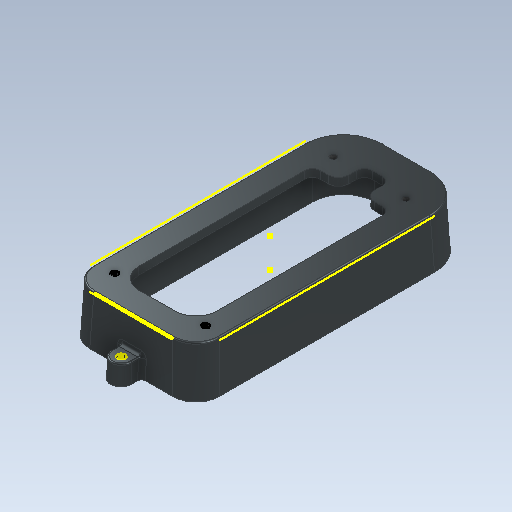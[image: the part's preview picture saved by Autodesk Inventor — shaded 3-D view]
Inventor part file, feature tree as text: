
AUTODESK INVENTOR PART (.ipt)
format: ipt  version: 2020 (Build 240168000, 168)  size: 400,896 bytes
history: native  units: mm
features: fillet x10, sketch x9, move_body x6, extrude x5, direct_edit x5, draft x5, thread x4, hole x2, boolean_combine x2, revolve x2, shell x1
ambient origin geometry x8: Origin, YZ Plane, XZ Plane, XY Plane, X Axis, Y Axis, Z Axis, Center Point
bodies: Solid1 (feature_tree), Solid2 (feature_tree), Solid3 (feature_tree)
feature tree (51):
  extrude  "Extrusion1"  Depth=107.0mm
  extrude  "Extrusion2"  Depth=8.0mm
  direct_edit  "Direct Edit1"
  draft  "FaceDraft1"
  draft  "FaceDraft2"
  direct_edit  "Direct Edit2"
  fillet  "Fillet1"  Radius=8.0mm
  direct_edit  "Direct Edit3"
  extrude  "Extrusion3"  Depth=7.5mm TaperAngle=0.0deg
  fillet  "Fillet2"  [1 undecoded]
  fillet  "Fillet3"  Radius=0.436332mm
  fillet  "Fillet4"  [1 undecoded]
  fillet  "Fillet5"  Radius=4.0mm
  fillet  "Fillet6"  Radius=30.0mm
  fillet  "Fillet7"  Radius=75.0mm
  sketch  "Sketch5"  dims[d10=0.0mm d11=0.0mm d12=5.0mm d13=0.436332mm d14=-0.436332mm]
  shell  "Shell1"  Thickness=10.0mm
  extrude  "Extrusion6"  Depth=10.0mm
  direct_edit  "Direct Edit4"
  draft  "FaceDraft3"
  draft  "FaceDraft4"
  draft  "FaceDraft5"
  direct_edit  "Direct Edit5"
  fillet  "Fillet13"  Radius=10.0mm
  hole  "Hole4"  [1 undecoded]
  sketch  "Sketch11"  dims[d25=10.0mm d26=10.0mm d27=10.0mm]
  extrude  "Extrusion7"  Depth=1.5mm
  fillet  "Fillet14"  Radius=8.0mm
  boolean_combine  "Combine4"
  boolean_combine  "Combine5"
  fillet  "Fillet15"  Radius=0.5mm
  hole  "Hole5"  [1 undecoded]
  thread  "Thread5"  [1 undecoded]
  thread  "Thread6"  [1 undecoded]
  thread  "Thread7"  [1 undecoded]
  thread  "Thread8"  [1 undecoded]
  sketch  "Sketch1"  dims[d0=50.0mm d1=107.0mm]
  sketch  "Sketch2"  dims[d2=19.0mm d3=-0.436332mm d4=8.0mm d5=8.0mm]
  sketch  "Sketch3"  dims[d6=4.0mm d7=7.5mm d8=0.0mm d9=-0.436332mm]
  sketch  "Sketch8"  dims[d15=0.0mm d16=-5.0mm d17=0.0mm d18=4.0mm]
  sketch  "Sketch10"  dims[d19=0.0mm d20=0.0mm d21=0.218097mm d22=30.0mm d23=75.0mm d24=10.0mm]
  sketch  "Sketch12"  dims[d28=0.0mm d29=3.0mm d30=0.0mm]
  sketch  "Sketch13"  dims[d31=4.0mm d32=3.0mm d33=8.0mm d34=0.5mm d35=9.0mm d36=15.0mm d48=2.5mm d49=2.5mm d50=35.0mm d53=7.5mm d54=7.5mm d65=3.0mm d85=8.0mm d86=8.0mm d87=0.0mm d88=7.5mm d89=0.0mm d90=0.436332mm d91=0.0mm d92=0.0mm d93=-0.174478mm d94=0.0mm d95=-4.0mm d96=0.0mm d97=-0.436332mm d98=0.436332mm d99=0.436332mm d100=0.0mm d101=4.0mm d102=0.0mm d118=4.0mm d119=115.0mm d120=57.5mm d121=57.5mm d122=3.0mm d123=6.0mm d124=4.0mm d125=2.0mm d126=90.0deg d127=8.0mm d128=20.594885mm d129=115.0mm d130=3.0mm d131=115.0mm d132=10.0mm d133=0.0mm d134=0.5mm d135=1.5mm d136=11.0mm d137=11.0mm d138=81.0mm d139=81.0mm d140=14.0mm d141=14.0mm d142=2.5mm d143=6.0mm d144=4.0mm d145=2.0mm d146=90.0deg d147=8.0mm d148=20.594885mm d149=3.0mm d150=0.0mm d151=3.0mm d152=0.0mm d153=3.0mm d154=0.0mm d155=3.0mm d156=0.0mm d75=0.5mm d76=0.872665mm d77=0.5mm d78=0.872665mm]
  revolve  "Rotate1"  [1 undecoded]
  move_body  "Move1"
  move_body  "Move2"
  move_body  "Move3"
  revolve  "Rotate2"  [1 undecoded]
  move_body  "Move4"
  move_body  "Move5"
  move_body  "Move6"
note: 10 required parameter values undecoded (feature->parameter linkage not recoverable at this tier; creation-order binding heuristic only, values carry confidence <= 0.55)